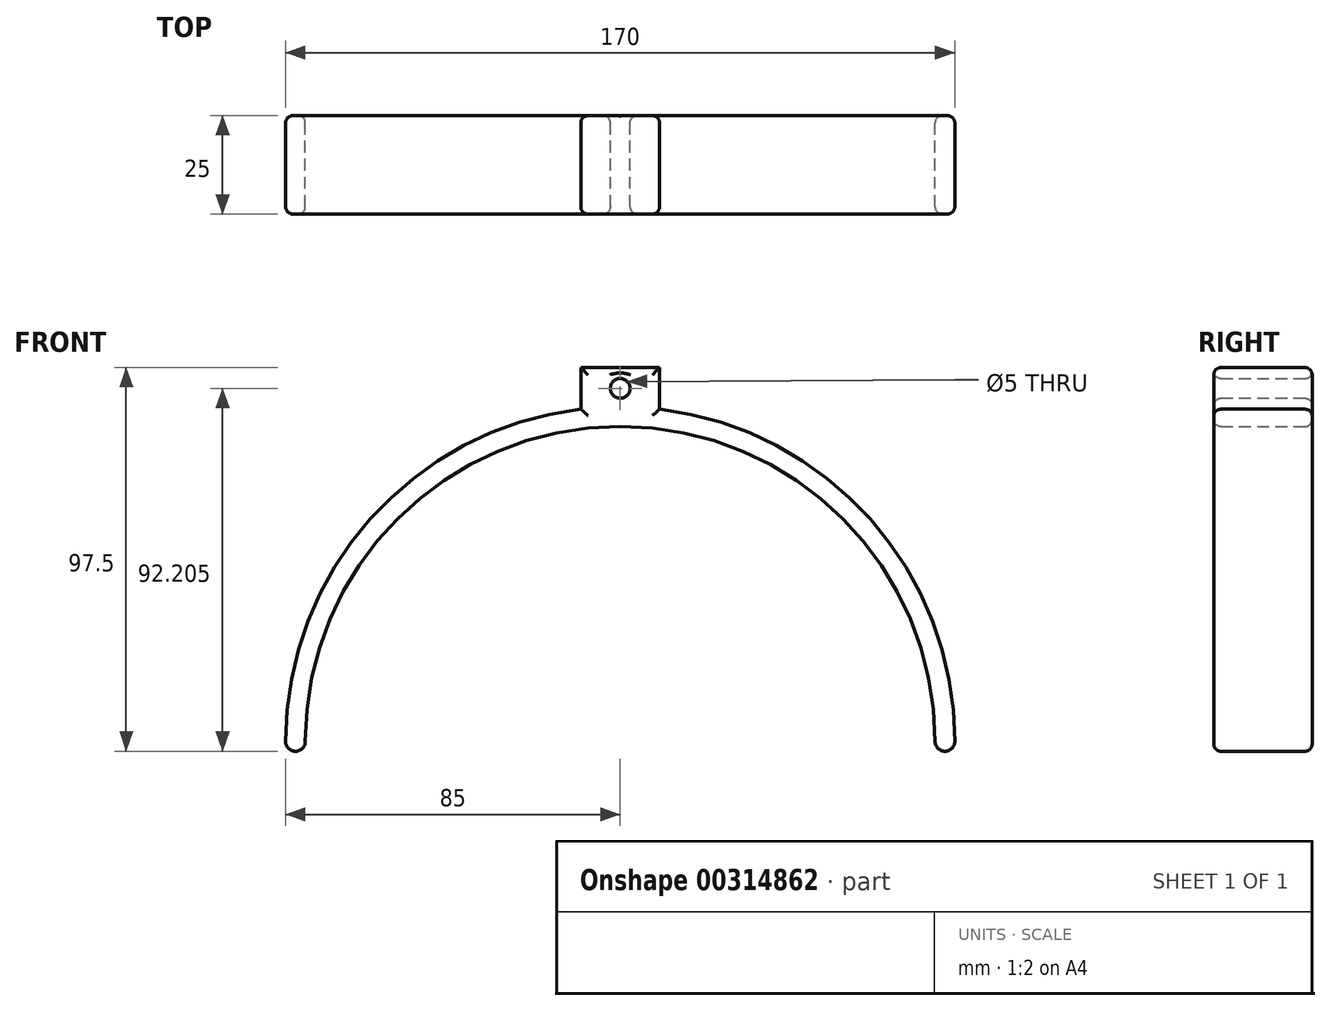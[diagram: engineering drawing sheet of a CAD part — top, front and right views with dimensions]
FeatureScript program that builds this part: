
annotation { "Feature Type Name" : "Feature", "Feature Type Description" : "" }
export const myFeature = defineFeature(function(context is Context, id is Id, definition is map)
    precondition{}
    {
        {
            var Q0;
            Q0=qCreatedBy(makeId("Front.planeOp"),FACE);
            var sketch = newSketch(context, id + "F0", { "sketchPlane" : qUnion([Q0])});
            skArc(sketch, "E0", {"start": v(80, 0) * mm, "mid": v(0, 80) * mm, "end": v(-80, 0) * mm});
            skArc(sketch, "E1", {"start": v(-10, 84.4) * mm, "mid": v(-63.54, 56.46) * mm, "end": v(-85, 0) * mm});
            skLineSegment(sketch, "E2", {"start": v(0, 0) * mm, "end": v(0, 95) * mm, "construction": true});
            skLineSegment(sketch, "E3", {"start": v(0, 95) * mm, "end": v(-10, 95) * mm});
            skLineSegment(sketch, "E4", {"start": v(0, 95) * mm, "end": v(10, 95) * mm});
            skLineSegment(sketch, "E5", {"start": v(-10, 95) * mm, "end": v(-10, 84.4) * mm});
            skLineSegment(sketch, "E6", {"start": v(10, 95) * mm, "end": v(10, 84.4) * mm});
            skLineSegment(sketch, "E7", {"start": v(-10, 84.4) * mm, "end": v(10, 95) * mm, "construction": true});
            skLineSegment(sketch, "E8", {"start": v(10, 84.4) * mm, "end": v(-10, 95) * mm, "construction": true});
            skCircle(sketch, "E9", {"center": v(0, 89.7) * mm, "radius": 2.5 * mm});
            skLineSegment(sketch, "E10", {"start": v(-80, 0) * mm, "end": v(-85, 0) * mm, "construction": true});
            skLineSegment(sketch, "E11", {"start": v(80, 0) * mm, "end": v(85, 0) * mm, "construction": true});
            skArc(sketch, "E12", {"start": v(-85, 0) * mm, "mid": v(-82.5, -2.5) * mm, "end": v(-80, 0) * mm});
            skArc(sketch, "E13", {"start": v(80, 0) * mm, "mid": v(82.5, -2.5) * mm, "end": v(85, 0) * mm});
            skArc(sketch, "E14.trimOffspring", {"start": v(85, 0) * mm, "mid": v(63.54, 56.46) * mm, "end": v(10, 84.4) * mm});
            skSolve(sketch);
        }
        {
            var Q0;
            Q0 = qSketchRegion(id + "F0", true);
            extrude(context, id + "F1", {"entities" : qUnion([Q0]), "depth" : 25 * mm});
        }
        {
            var Q0;
            Q0=makeQuery(id+"F1.opExtrude","CAP_FACE",FACE,{"disambiguationData":[OSD([sQuery(id+"F0.wireOp",EDGE,"E0"),sQuery(id+"F0.wireOp",EDGE,"E1"),sQuery(id+"F0.wireOp",EDGE,"E3"),sQuery(id+"F0.wireOp",EDGE,"E4"),sQuery(id+"F0.wireOp",EDGE,"E5"),sQuery(id+"F0.wireOp",EDGE,"E6"),sQuery(id+"F0.wireOp",EDGE,"E9"),sQuery(id+"F0.wireOp",EDGE,"E12"),sQuery(id+"F0.wireOp",EDGE,"E13"),sQuery(id+"F0.wireOp",EDGE,"E14.trimOffspring")])],"isStart":false});
            var Q1;
            Q1=makeQuery(id+"F1.opExtrude","CAP_FACE",FACE,{"disambiguationData":[OSD([sQuery(id+"F0.wireOp",EDGE,"E0"),sQuery(id+"F0.wireOp",EDGE,"E1"),sQuery(id+"F0.wireOp",EDGE,"E3"),sQuery(id+"F0.wireOp",EDGE,"E4"),sQuery(id+"F0.wireOp",EDGE,"E5"),sQuery(id+"F0.wireOp",EDGE,"E6"),sQuery(id+"F0.wireOp",EDGE,"E9"),sQuery(id+"F0.wireOp",EDGE,"E12"),sQuery(id+"F0.wireOp",EDGE,"E13"),sQuery(id+"F0.wireOp",EDGE,"E14.trimOffspring")])],"isStart":true});
            fillet(context, id + "F2", {"entities" : qUnion([Q0, Q1]), "radius" : 1.84 * mm, "tangentPropagation" : true, "allowEdgeOverflow" : false});
        }
    });
